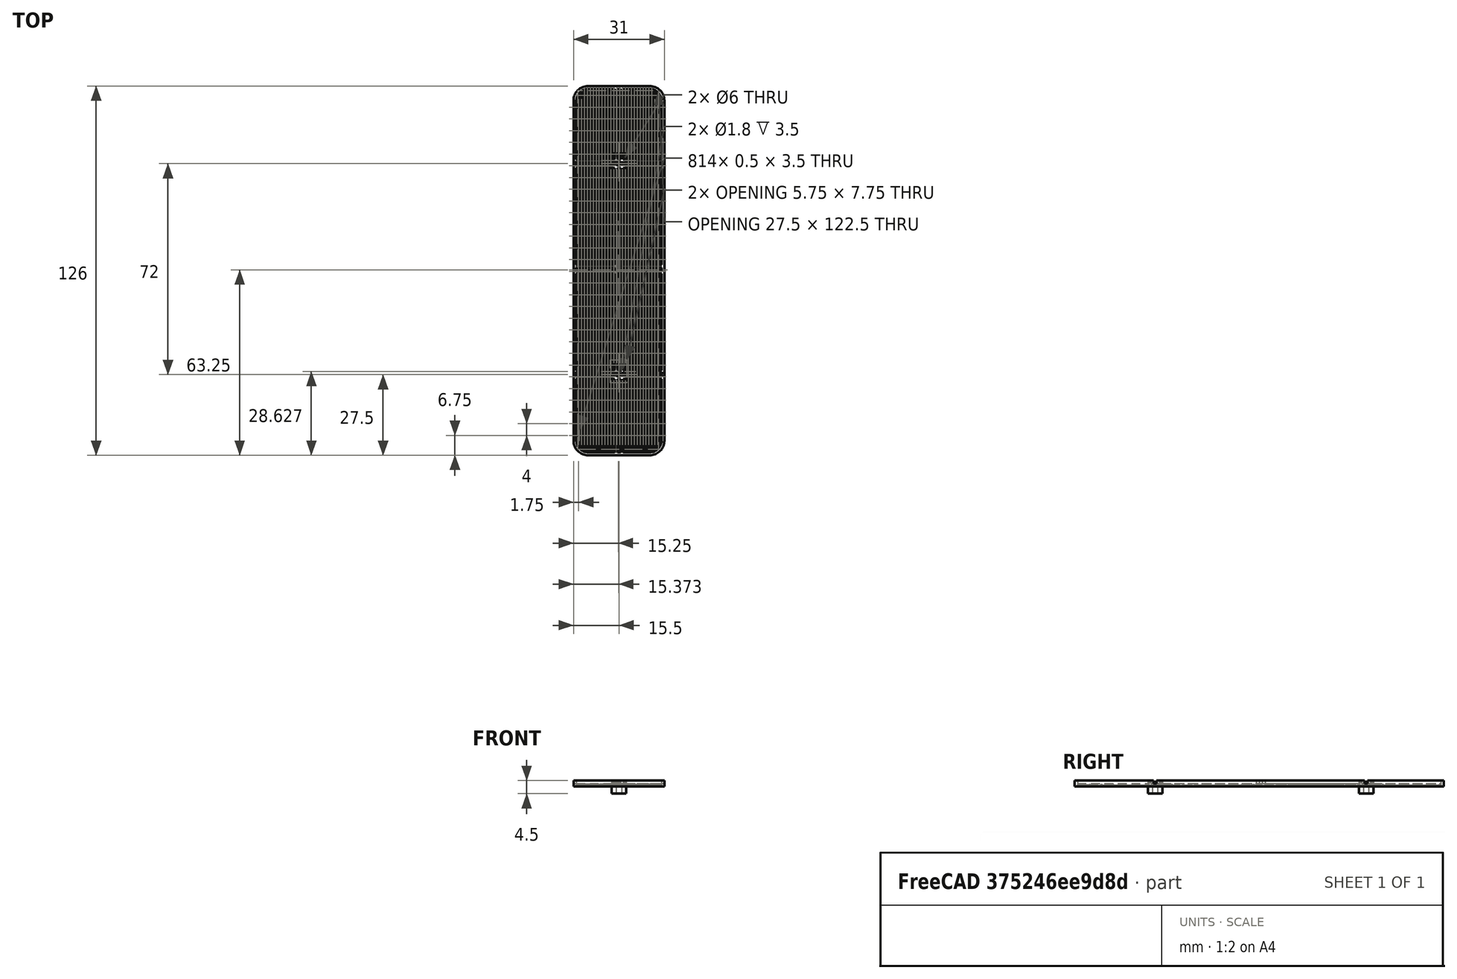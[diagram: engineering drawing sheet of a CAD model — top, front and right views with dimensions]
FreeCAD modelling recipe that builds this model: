
FCSTD DOCUMENT  (FreeCAD 0.14R3653 (Git))
Label: Cam-radiator-mask
License: CC-BY 3.0
LicenseURL: http://creativecommons.org/licenses/by/3.0/
objects: Part::Box×50, Part::MultiFuse×23, Part::Cut×10, Part::Fillet×7, Part::Cylinder×2
note: 92 computed .brp shape members not serialized (recipe doc carries the construction recipe); baked Part::Feature solids carry a one-line shape summary decoded from their .brp

FEATURE [Part::Cut] Cut
FEATURE [Part::MultiFuse] Fusion
FEATURE [Part::Cut] Cut001  label="radiator-grid"
  Base = -> Cut
  Placement = pos=(0,0,2) rot=(0,1,0;1.5708rad)
  Tool = -> Fusion
FEATURE [Part::Cut] Cut002
FEATURE [Part::MultiFuse] Fusion002
  Placement = pos=(-0.5,0,0) rot=(0,0,1;0rad)
FEATURE [Part::Cut] Cut003
FEATURE [Part::MultiFuse] Fusion001  label="radiator-mask"
  Placement = pos=(0,0,2) rot=(0,1,0;1.5708rad)
  Shapes = -> [Cut002,Fusion002,Cut003]
FEATURE [Part::Box] Box  label="Cube"
  Height = 0.5
  Length = 27.5
  Placement = pos=(8.5,22,0) rot=(0,0,1;0rad)
  Width = 123.5
FEATURE [Part::Fillet] Fillet
  Base = -> Box
  Edges = 4 edges r=4: [Edge1,Edge3,Edge5,Edge7]
FEATURE [Part::Box] Box004  label="Cube001"
  Height = 0.5
  Length = 26
  Placement = pos=(9,23,0) rot=(0,0,1;0rad)
  Width = 122
FEATURE [Part::Fillet] Fillet001
  Base = -> Box004
  Edges = 4 edges r=3: [Edge1,Edge3,Edge5,Edge7]
FEATURE [Part::Box] Box005  label="Cube002"
  Height = 0.5
  Length = 29.5
  Placement = pos=(8,22,0) rot=(0,0,1;0rad)
  Width = 124.5
FEATURE [Part::Fillet] Fillet002
  Base = -> Box005
  Edges = 4 edges r=4: [Edge1,Edge3,Edge5,Edge7]
  Placement = pos=(-0.5,0,0) rot=(0,0,1;0rad)
FEATURE [Part::Box] Box006  label="Cube003"
  Height = 0.5
  Length = 28.5
  Placement = pos=(8.5,22.5,0) rot=(0,0,1;0rad)
  Width = 123.5
FEATURE [Part::Fillet] Fillet003
  Base = -> Box006
  Edges = 4 edges r=3.5: [Edge1,Edge3,Edge5,Edge7]
  Placement = pos=(-0.5,0,0) rot=(0,0,1;0rad)
FEATURE [Part::Cut] Cut004
  Base = -> Fillet002
  Tool = -> Fillet003
FEATURE [Part::Box] Box007  label="Cube004"
  Height = 0.5
  Length = 28.5
  Placement = pos=(8.5,22.5,0) rot=(0,0,1;0rad)
  Width = 123.5
FEATURE [Part::Fillet] Fillet004
  Base = -> Box007
  Edges = 4 edges r=3.5: [Edge1,Edge3,Edge5,Edge7]
  Placement = pos=(-0.5,0,0) rot=(0,0,1;0rad)
FEATURE [Part::Box] Box008  label="Cube005"
  Height = 0.5
  Length = 27.5
  Placement = pos=(8,22,0) rot=(0,0,1;0rad)
  Width = 122.5
FEATURE [Part::Fillet] Fillet005
  Base = -> Box008
  Edges = 4 edges r=3: [Edge1,Edge3,Edge5,Edge7]
  Placement = pos=(0.5,1,0) rot=(0,0,1;0rad)
FEATURE [Part::Cut] Cut005
  Base = -> Fillet004
  Tool = -> Fillet005
FEATURE [Part::Cut] Cut006
  Base = -> Cut001
  Tool = -> Cut004
FEATURE [Part::Box] Box009  label="Cube006"
  Height = 0.2
  Length = 0.4
  Placement = pos=(36.5,22,0) rot=(0,0,1;0rad)
  Width = 124
FEATURE [Part::Box] Box010  label="Cube007"
  Height = 0.2
  Length = 0.4
  Placement = pos=(35.5,22,0) rot=(0,0,1;0rad)
  Width = 124
FEATURE [Part::Box] Box011  label="Cube008"
  Height = 0.2
  Length = 0.4
  Placement = pos=(34.5,22,0) rot=(0,0,1;0rad)
  Width = 124
FEATURE [Part::Box] Box012  label="Cube009"
  Height = 0.2
  Length = 0.4
  Placement = pos=(33.5,22,0) rot=(0,0,1;0rad)
  Width = 124
FEATURE [Part::MultiFuse] Fusion003
  Shapes = -> [Box009,Box010,Box012,Box011]
FEATURE [Part::Box] Box013  label="Cube010"
  Height = 0.2
  Length = 0.4
  Placement = pos=(36.5,22,0) rot=(0,0,1;0rad)
  Width = 124
FEATURE [Part::Box] Box014  label="Cube011"
  Height = 0.2
  Length = 0.4
  Placement = pos=(33.5,22,0) rot=(0,0,1;0rad)
  Width = 124
FEATURE [Part::Box] Box015  label="Cube012"
  Height = 0.2
  Length = 0.4
  Placement = pos=(34.5,22,0) rot=(0,0,1;0rad)
  Width = 124
FEATURE [Part::Box] Box016  label="Cube013"
  Height = 0.2
  Length = 0.4
  Placement = pos=(35.5,22,0) rot=(0,0,1;0rad)
  Width = 124
FEATURE [Part::MultiFuse] Fusion004
  Placement = pos=(-4,0,0) rot=(0,0,1;0rad)
  Shapes = -> [Box013,Box016,Box014,Box015]
FEATURE [Part::Box] Box017  label="Cube014"
  Height = 0.2
  Length = 0.4
  Placement = pos=(36.5,22,0) rot=(0,0,1;0rad)
  Width = 124
FEATURE [Part::Box] Box018  label="Cube015"
  Height = 0.2
  Length = 0.4
  Placement = pos=(33.5,22,0) rot=(0,0,1;0rad)
  Width = 124
FEATURE [Part::Box] Box019  label="Cube016"
  Height = 0.2
  Length = 0.4
  Placement = pos=(34.5,22,0) rot=(0,0,1;0rad)
  Width = 124
FEATURE [Part::Box] Box020  label="Cube017"
  Height = 0.2
  Length = 0.4
  Placement = pos=(35.5,22,0) rot=(0,0,1;0rad)
  Width = 124
FEATURE [Part::MultiFuse] Fusion005
  Placement = pos=(-8,0,0) rot=(0,0,1;0rad)
  Shapes = -> [Box017,Box020,Box018,Box019]
FEATURE [Part::Box] Box021  label="Cube018"
  Height = 0.2
  Length = 0.4
  Placement = pos=(35.5,22,0) rot=(0,0,1;0rad)
  Width = 124
FEATURE [Part::Box] Box022  label="Cube019"
  Height = 0.2
  Length = 0.4
  Placement = pos=(34.5,22,0) rot=(0,0,1;0rad)
  Width = 124
FEATURE [Part::Box] Box023  label="Cube020"
  Height = 0.2
  Length = 0.4
  Placement = pos=(36.5,22,0) rot=(0,0,1;0rad)
  Width = 124
FEATURE [Part::Box] Box024  label="Cube021"
  Height = 0.2
  Length = 0.4
  Placement = pos=(33.5,22,0) rot=(0,0,1;0rad)
  Width = 124
FEATURE [Part::MultiFuse] Fusion006
  Placement = pos=(-12,0,0) rot=(0,0,1;0rad)
  Shapes = -> [Box023,Box021,Box024,Box022]
FEATURE [Part::Box] Box025  label="Cube022"
  Height = 0.2
  Length = 0.4
  Placement = pos=(36.5,22,0) rot=(0,0,1;0rad)
  Width = 124
FEATURE [Part::Box] Box026  label="Cube023"
  Height = 0.2
  Length = 0.4
  Placement = pos=(34.5,22,0) rot=(0,0,1;0rad)
  Width = 124
FEATURE [Part::Box] Box027  label="Cube024"
  Height = 0.2
  Length = 0.4
  Placement = pos=(33.5,22,0) rot=(0,0,1;0rad)
  Width = 124
FEATURE [Part::Box] Box028  label="Cube025"
  Height = 0.2
  Length = 0.4
  Placement = pos=(35.5,22,0) rot=(0,0,1;0rad)
  Width = 124
FEATURE [Part::MultiFuse] Fusion007
  Placement = pos=(-16,0,0) rot=(0,0,1;0rad)
  Shapes = -> [Box025,Box028,Box027,Box026]
FEATURE [Part::Box] Box029  label="Cube026"
  Height = 0.2
  Length = 0.4
  Placement = pos=(33.5,22,0) rot=(0,0,1;0rad)
  Width = 124
FEATURE [Part::Box] Box030  label="Cube027"
  Height = 0.2
  Length = 0.4
  Placement = pos=(34.5,22,0) rot=(0,0,1;0rad)
  Width = 124
FEATURE [Part::Box] Box031  label="Cube028"
  Height = 0.2
  Length = 0.4
  Placement = pos=(35.5,22,0) rot=(0,0,1;0rad)
  Width = 124
FEATURE [Part::Box] Box032  label="Cube029"
  Height = 0.2
  Length = 0.4
  Placement = pos=(36.5,22,0) rot=(0,0,1;0rad)
  Width = 124
FEATURE [Part::MultiFuse] Fusion008
  Placement = pos=(-20,0,0) rot=(0,0,1;0rad)
  Shapes = -> [Box032,Box031,Box029,Box030]
FEATURE [Part::Box] Box033  label="Cube030"
  Height = 0.2
  Length = 0.4
  Placement = pos=(36.5,22,0) rot=(0,0,1;0rad)
  Width = 124
FEATURE [Part::Box] Box034  label="Cube031"
  Height = 0.2
  Length = 0.4
  Placement = pos=(34.5,22,0) rot=(0,0,1;0rad)
  Width = 124
FEATURE [Part::Box] Box035  label="Cube032"
  Height = 0.2
  Length = 0.4
  Placement = pos=(33.5,22,0) rot=(0,0,1;0rad)
  Width = 124
FEATURE [Part::Box] Box036  label="Cube033"
  Height = 0.2
  Length = 0.4
  Placement = pos=(35.5,22,0) rot=(0,0,1;0rad)
  Width = 124
FEATURE [Part::MultiFuse] Fusion009
  Placement = pos=(-24,0,0) rot=(0,0,1;0rad)
  Shapes = -> [Box033,Box036,Box035,Box034]
FEATURE [Part::Box] Box037  label="Cube034"
  Height = 0.2
  Length = 0.4
  Placement = pos=(8.5,22,0) rot=(0,0,1;0rad)
  Width = 124
FEATURE [Part::MultiFuse] Fusion010
  Shapes = -> [Fusion003,Fusion005,Fusion007,Fusion006,Fusion008,Fusion009,Box037,Fusion004]
FEATURE [Part::Box] Box038  label="Cube035"
  Height = 0.2
  Length = 28.5
  Placement = pos=(8.5,22,0.3) rot=(0,0,1;0rad)
  Width = 0.4
FEATURE [Part::Box] Box039  label="Cube036"
  Height = 0.2
  Length = 28.5
  Placement = pos=(8.5,26,0.3) rot=(0,0,1;0rad)
  Width = 0.4
FEATURE [Part::Box] Box040  label="Cube037"
  Height = 0.2
  Length = 28.5
  Placement = pos=(8.5,30,0.3) rot=(0,0,1;0rad)
  Width = 0.4
FEATURE [Part::Box] Box041  label="Cube038"
  Height = 0.2
  Length = 28.5
  Placement = pos=(8.5,34,0.3) rot=(0,0,1;0rad)
  Width = 0.4
FEATURE [Part::Box] Box042  label="Cube039"
  Height = 0.2
  Length = 28.5
  Placement = pos=(8.5,38,0.3) rot=(0,0,1;0rad)
  Width = 0.4
FEATURE [Part::MultiFuse] Fusion011
  Shapes = -> [Box038,Box041,Box042,Box040,Box039]
FEATURE [Part::Box] Box043  label="Cube040"
  Height = 0.2
  Length = 28.5
  Placement = pos=(8.5,30,0.3) rot=(0,0,1;0rad)
  Width = 0.4
FEATURE [Part::Box] Box044  label="Cube041"
  Height = 0.2
  Length = 28.5
  Placement = pos=(8.5,26,0.3) rot=(0,0,1;0rad)
  Width = 0.4
FEATURE [Part::Box] Box045  label="Cube042"
  Height = 0.2
  Length = 28.5
  Placement = pos=(8.5,34,0.3) rot=(0,0,1;0rad)
  Width = 0.4
FEATURE [Part::Box] Box046  label="Cube043"
  Height = 0.2
  Length = 28.5
  Placement = pos=(8.5,22,0.3) rot=(0,0,1;0rad)
  Width = 0.4
FEATURE [Part::Box] Box047  label="Cube044"
  Height = 0.2
  Length = 28.5
  Placement = pos=(8.5,38,0.3) rot=(0,0,1;0rad)
  Width = 0.4
FEATURE [Part::MultiFuse] Fusion012
  Placement = pos=(0,20,0) rot=(0,0,1;0rad)
  Shapes = -> [Box046,Box045,Box047,Box043,Box044]
FEATURE [Part::MultiFuse] Fusion013
  Placement = pos=(0,40,0) rot=(0,0,1;0rad)
  Shapes = -> [Fusion011,Fusion012]
FEATURE [Part::MultiFuse] Fusion014
  Placement = pos=(0,20,0) rot=(0,0,1;0rad)
  Shapes = -> [Box046,Box045,Box047,Box043,Box044]
FEATURE [Part::MultiFuse] Fusion016
  Shapes = -> [Box038,Box041,Box042,Box040,Box039]
FEATURE [Part::MultiFuse] Fusion015
  Shapes = -> [Fusion016,Fusion014]
FEATURE [Part::MultiFuse] Fusion017
  Placement = pos=(0,20,0) rot=(0,0,1;0rad)
  Shapes = -> [Box046,Box045,Box047,Box043,Box044]
FEATURE [Part::MultiFuse] Fusion019
  Shapes = -> [Box038,Box041,Box042,Box040,Box039]
FEATURE [Part::MultiFuse] Fusion018
  Placement = pos=(0,80,0) rot=(0,0,1;0rad)
  Shapes = -> [Fusion019,Fusion017]
FEATURE [Part::Box] Box048  label="Cube045"
  Height = 0.2
  Length = 28.5
  Placement = pos=(8.5,142,0.3) rot=(0,0,1;0rad)
  Width = 0.4
FEATURE [Part::Box] Box049  label="Cube046"
  Height = 0.2
  Length = 28.5
  Placement = pos=(8.5,145.5,0.3) rot=(0,0,1;0rad)
  Width = 0.4
FEATURE [Part::MultiFuse] Fusion020
  Placement = pos=(0,0,0.2) rot=(0,0,1;0rad)
  Shapes = -> [Fusion010,Box048,Fusion018,Fusion013,Box049,Fusion015]
FEATURE [Part::Box] Box050  label="Cube047"
  Height = 10
  Length = 28.5
  Placement = pos=(8.25,22.25,0) rot=(0,0,1;0rad)
  Width = 123.5
FEATURE [Part::Fillet] Fillet006
  Base = -> Box050
  Edges = 4 edges r=4: [Edge1,Edge3,Edge5,Edge7]
FEATURE [Part::Box] Box051  label="Cube048"
  Height = 10
  Length = 31
  Placement = pos=(7,21,0) rot=(0,0,1;0rad)
  Width = 126
FEATURE [Part::Cut] Cut007
  Base = -> Box051
  Tool = -> Fillet006
FEATURE [Part::Cylinder] Cylinder
  Angle = 360
  Height = 10
  Placement = pos=(22.5,48.5,-3) rot=(0,0,1;0rad)
  Radius = 3
FEATURE [Part::Cylinder] Cylinder001
  Angle = 360
  Height = 10
  Placement = pos=(22.5,120.5,-3) rot=(0,0,1;0rad)
  Radius = 3
FEATURE [Part::MultiFuse] Fusion021
  Shapes = -> [Cylinder,Cylinder001]
FEATURE [Part::Box] Box052  label="Cube049"
  Height = 0.1
  Length = 28.5
  Placement = pos=(8.25,22.25,0) rot=(0,0,1;0rad)
  Width = 123.5
FEATURE [Part::MultiFuse] Fusion022
  Shapes = -> [Fusion020,Box052]
FEATURE [Part::Cut] Cut008
  Base = -> Fusion022
  Tool = -> Cut007
FEATURE [Part::Cut] Cut009
  Base = -> Cut008
  Tool = -> Fusion021
